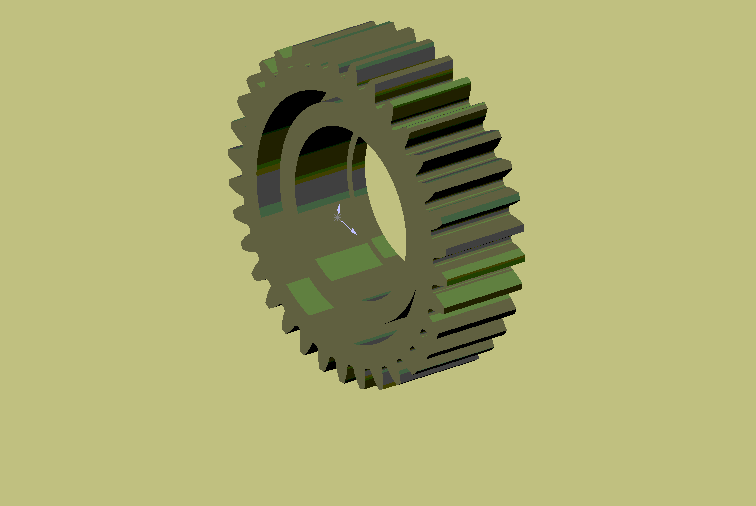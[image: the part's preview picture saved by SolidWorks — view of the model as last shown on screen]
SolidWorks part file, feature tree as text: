
SOLIDWORKS PART (.sldprt)
format: sldprt  version: not decoded by parser v0  size: 502,272 bytes
history: native  units: mm
features: sketch x22, plane x4, cut_extrude x4, material x1, fillet x1, pattern_circular x1 + 1 further entry (+9 scaffold rows collapsed)
feature tree (43):
  scaffold x9  (default folders/planes/origin — collapsed)
  material  "Matériau <non spécifié>"
  plane  "Plane1"
  plane  "Plane2"
  plane  "Plane3"
  "Famille de pièces"
  sketch  "Esquisse1"  dims[c1.D2=10.2mm c1.D1=42.0mm c2.D1=~5.294118deg]
  sketch  "Esquisse2"  dims[c1.D2=~9.994955mm c1.D1=37.0mm c2.D1=~6.063792deg]
  sketch  "Esquisse3"  dims[c1.D2=~9.78991mm c1.D1=33.0mm c2.D1=~6.667199deg]
  sketch  "Esquisse4"  dims[c1.D2=~9.584865mm c1.D1=30.0mm c2.D1=~7.002034deg]
  sketch  "Esquisse5"  dims[c1.D2=10.4mm c1.D1=46.0mm c2.D1=~4.419544deg]
  sketch  "Esquisse6"  dims[c1.D2=10.6mm c1.D1=50.0mm c2.D1=~3.443833deg]
  sketch  "Esquisse7"  dims[c1.D2=10.8mm c1.D1=54.0mm c2.D1=~2.38145deg]
  plane  "Plan1"  Offset=6mm
  sketch  "Esquisse8"  dims[c1.D2=10.2mm c1.D1=18.0mm c2.D1=~5.294118deg]
  sketch  "Esquisse9"  dims[c1.D2=~9.994955mm c1.D1=15.0mm c2.D1=~6.063792deg]
  sketch  "Esquisse10"  dims[c1.D2=~9.78991mm c1.D1=13.0mm c2.D1=~6.667199deg]
  sketch  "Esquisse11"  dims[c1.D2=~9.584865mm c1.D1=12.0mm c2.D1=~7.002034deg]
  sketch  "Esquisse12"  dims[c1.D2=10.4mm c1.D1=20.0mm c2.D1=~4.419544deg]
  sketch  "Esquisse13"  dims[c1.D2=10.6mm c1.D1=21.0mm c2.D1=~3.443833deg]
  sketch  "Esquisse14"  dims[c1.D2=10.8mm c1.D1=22.0mm c2.D1=~2.38145deg]
  sketch  "Esquisse15"  dims[c1.D2=9.45mm c1.D1=23.0mm c2.D1=~7.002034deg]
  sketch  "Esquisse16"  dims[c1.D2=9.45mm c1.D1=10.0mm c2.D1=~7.002034deg]
  sketch  "Esquisse17"  dims[D1=18.9mm]
  sketch  "Esquisse18"  dims[D1=18.9mm]
  fillet  "Congé1"  Radius=0.25mm
  pattern_circular  "Répétition circulaire1"  Count=34 Angle=360deg
  sketch  "Esquisse19"  dims[D1=16.0mm]
  cut_extrude  "Enlèv. mat.-Extru.1"  Depth=1mm
  sketch  "Esquisse20"  dims[D1=~9.665652mm]
  cut_extrude  "Enlèv. mat.-Extru.2"  [1 undecoded]
  sketch  "Esquisse21"  dims[D1=11.0mm D2=14.0mm]
  cut_extrude  "Enlèv. mat.-Extru.3"  Depth=4mm
  sketch  "Esquisse22"  dims[D1=14.0mm]
  cut_extrude  "Enlèv. mat.-Extru.4"  Depth=3mm
decode coverage: 27 of 28 modeling features carry decoded parameters; 1 rows unclassified (native names shown)
note: ~ marks probable driven/reference dimensions
note: 1 parameter value undecoded
note: suppression state not decoded; provenance and decode notes live in map.json
